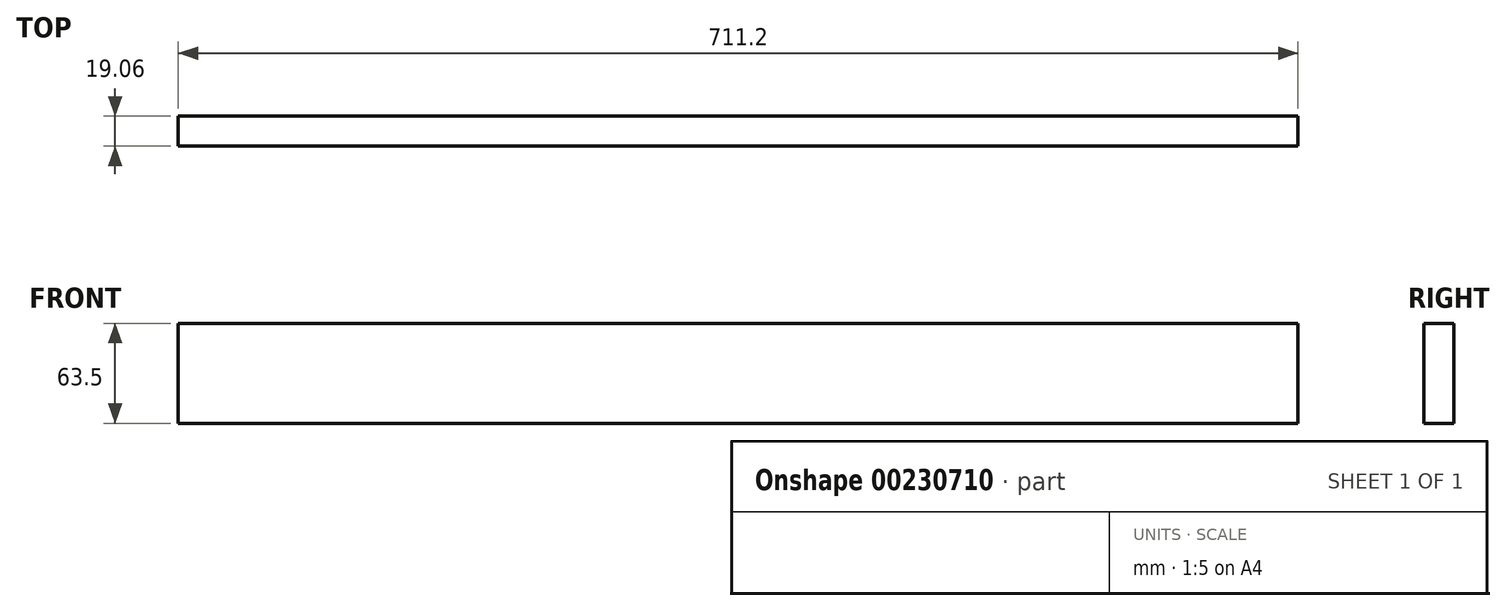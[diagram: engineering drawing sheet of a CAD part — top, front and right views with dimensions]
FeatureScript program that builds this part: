
annotation { "Feature Type Name" : "Feature", "Feature Type Description" : "" }
export const myFeature = defineFeature(function(context is Context, id is Id, definition is map)
    precondition{}
    {
        {
            var Q0;
            Q0=qCreatedBy(makeId("Right.planeOp"),FACE);
            var sketch = newSketch(context, id + "F0", { "sketchPlane" : qUnion([Q0])});
            skLineSegment(sketch, "E0.bottom", {"start": v(-9.52, 44.45) * mm, "end": v(9.53, 44.45) * mm});
            skLineSegment(sketch, "E0.top", {"start": v(-9.52, -19.05) * mm, "end": v(9.53, -19.05) * mm});
            skLineSegment(sketch, "E0.left", {"start": v(-9.52, 44.45) * mm, "end": v(-9.52, -19.05) * mm});
            skLineSegment(sketch, "E0.right", {"start": v(9.53, 44.45) * mm, "end": v(9.53, -19.05) * mm});
            skSolve(sketch);
        }
        {
            var Q0;
            Q0=makeQuery(id+"F0.imprint","IMPRINT",FACE,{"disambiguationData":[TD([[makeQuery(id+"F0.imprint","IMPRINT",EDGE,{"derivedFrom":sQuery(id+"F0.wireOp",EDGE,"E0.bottom")}),-1.0]])]});
            extrude(context, id + "F1", {"entities" : qUnion([Q0]), "depth" : 711.2 * mm});
        }
    });
